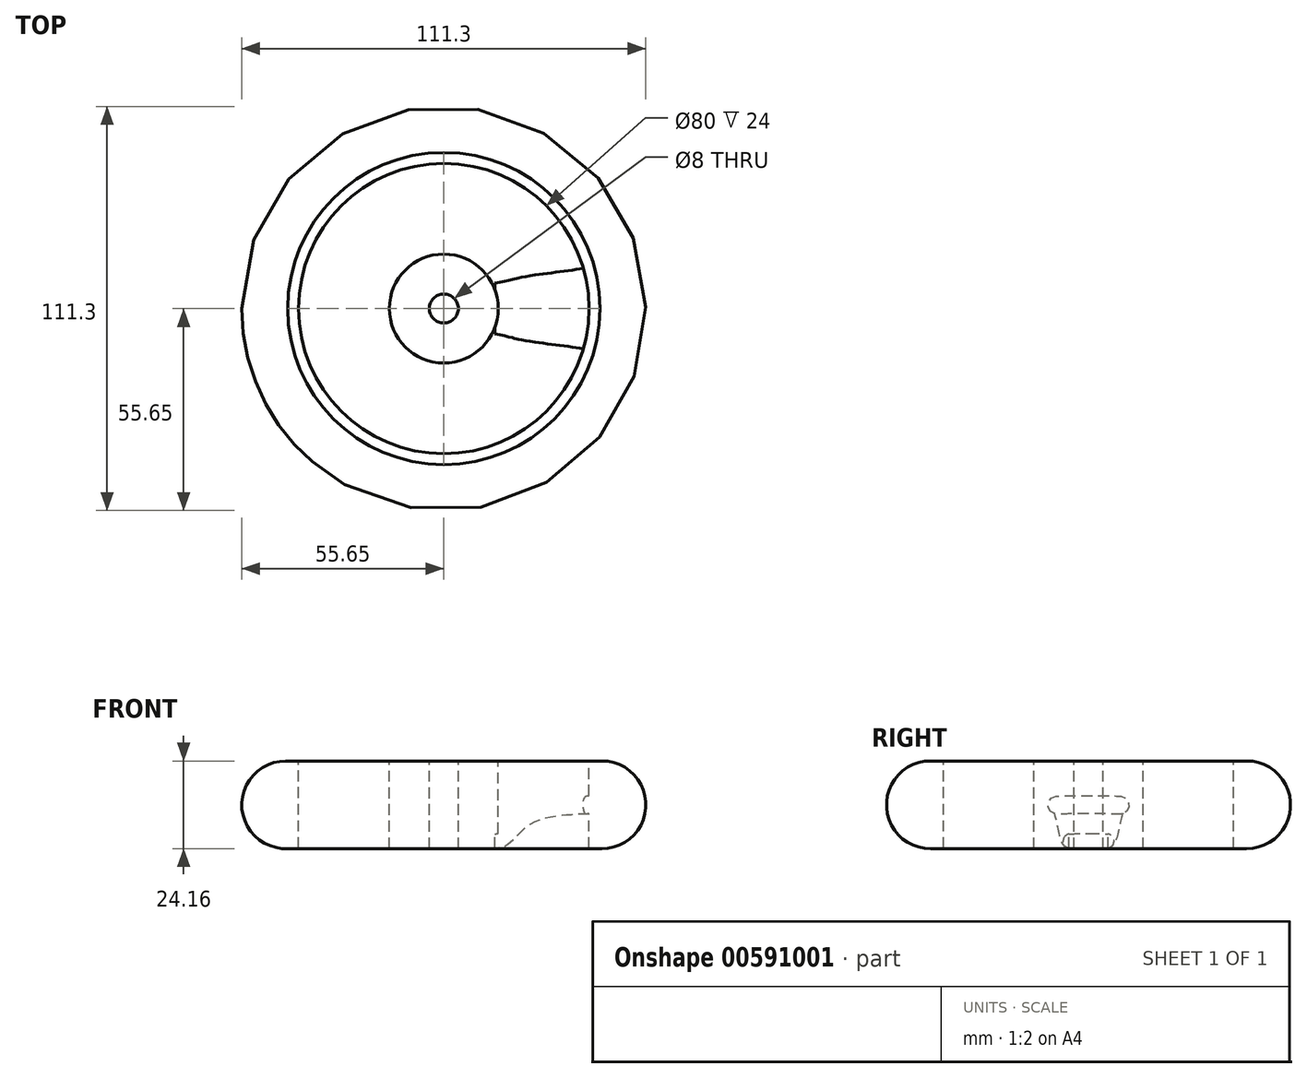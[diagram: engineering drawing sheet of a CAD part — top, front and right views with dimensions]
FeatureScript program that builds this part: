
annotation { "Feature Type Name" : "Feature", "Feature Type Description" : "" }
export const myFeature = defineFeature(function(context is Context, id is Id, definition is map)
    precondition{}
    {
        {
            var Q0;
            Q0=qCreatedBy(makeId("Top.planeOp"),FACE);
            var sketch = newSketch(context, id + "F0", { "sketchPlane" : qUnion([Q0])});
            skCircle(sketch, "E0", {"center": v(0, 0) * mm, "radius": 40 * mm});
            skSolve(sketch);
        }
        {
            var Q0;
            Q0=qCreatedBy(makeId("Front.planeOp"),FACE);
            var sketch = newSketch(context, id + "F1", { "sketchPlane" : qUnion([Q0])});
            skArc(sketch, "E1", {"start": v(-43, 12.07) * mm, "mid": v(-55.65, 0) * mm, "end": v(-43, -12.07) * mm});
            skLineSegment(sketch, "E2", {"start": v(-43, 12.07) * mm, "end": v(-40, 12.07) * mm});
            skLineSegment(sketch, "E3", {"start": v(-40, 12.07) * mm, "end": v(-40, -11.93) * mm});
            skLineSegment(sketch, "E4", {"start": v(-40, -11.93) * mm, "end": v(-43, -12.07) * mm});
            skSolve(sketch);
        }
        {
            var Q0;
            Q0 = qSketchRegion(id + "F1", true);
            var Q1;
            Q1 = qConstructionFilter(qBodyType(qCreatedBy(id + "F0" ,EDGE), BodyType.WIRE), ConstructionObject.NO);
            sweep(context, id + "F2", {"profiles" : qUnion([Q0]), "path" : qUnion([Q1])});
        }
        {
            var Q0;
            Q0=qCreatedBy(makeId("Right.planeOp"),FACE);
            cPlane(context, id + "F3", {"entities" : qUnion([Q0]), "cplaneType" : CPlaneType.OFFSET, "offset" : 40 * mm, "width" : 150 * mm, "height" : 150 * mm});
        }
        {
            var Q0;
            Q0=qCreatedBy(makeId("Right.planeOp"),FACE);
            cPlane(context, id + "F4", {"entities" : qUnion([Q0]), "cplaneType" : CPlaneType.OFFSET, "offset" : 14 * mm, "width" : 150 * mm, "height" : 150 * mm});
        }
        {
            var Q0;
            Q0=qCreatedBy(id+"F3.planeOp",FACE);
            var sketch = newSketch(context, id + "F5", { "sketchPlane" : qUnion([Q0])});
            skLineSegment(sketch, "E5", {"start": v(-9, 0) * mm, "end": v(9, 0) * mm});
            skArc(sketch, "E6.0.startCap", {"start": v(-9, -2.5) * mm, "mid": v(-11.5, 0) * mm, "end": v(-9, 2.5) * mm});
            skArc(sketch, "E6.0.endCap", {"start": v(9, 2.5) * mm, "mid": v(11.5, 0) * mm, "end": v(9, -2.5) * mm});
            skLineSegment(sketch, "E6.0.left", {"start": v(-9, 2.5) * mm, "end": v(9, 2.5) * mm});
            skLineSegment(sketch, "E6.0.right", {"start": v(-9, -2.5) * mm, "end": v(9, -2.5) * mm});
            skSolve(sketch);
        }
        {
            var Q0;
            Q0=qCreatedBy(id+"F4.planeOp",FACE);
            var sketch = newSketch(context, id + "F6", { "sketchPlane" : qUnion([Q0])});
            skLineSegment(sketch, "E7", {"start": v(-5, -10) * mm, "end": v(5, -10) * mm});
            skArc(sketch, "E8.0.startCap", {"start": v(-5, -12) * mm, "mid": v(-7, -10) * mm, "end": v(-5, -8) * mm});
            skArc(sketch, "E8.0.endCap", {"start": v(5, -8) * mm, "mid": v(7, -10) * mm, "end": v(5, -12) * mm});
            skLineSegment(sketch, "E8.0.left", {"start": v(-5, -8) * mm, "end": v(5, -8) * mm});
            skLineSegment(sketch, "E8.0.right", {"start": v(-5, -12) * mm, "end": v(5, -12) * mm});
            skSolve(sketch);
        }
        {
            var Q0;
            Q0=qCreatedBy(makeId("Front.planeOp"),FACE);
            var sketch = newSketch(context, id + "F7", { "sketchPlane" : qUnion([Q0])});
            skFitSpline(sketch, "E9", {"points": [v(14, -12) * mm, v(18.37, -10.38) * mm, v(24.16, -5.17) * mm, v(34.82, -2.8) * mm, v(40, -2.5) * mm], "startDerivative": vector(27.3, -0.01) * mm, "endDerivative": vector(15.84, 0.13) * mm});
            skSolve(sketch);
        }
        {
            var Q1;
            Q1 = qSketchRegion(id + "F5", true);
            var Q2;
            Q2 = qSketchRegion(id + "F6", true);
            var Q3;
            Q3 = qConstructionFilter(qBodyType(qCreatedBy(id + "F7" ,EDGE), BodyType.WIRE), ConstructionObject.NO);
            loft(context, id + "F8", {"operationType" : NewBodyOperationType.ADD, "addGuides" : true, "sheetProfilesArray" : [{ "sheetProfileEntities" : qUnion([Q1]) }, { "sheetProfileEntities" : qUnion([Q2]) }], "guidesArray" : [{ "guideEntities" : qUnion([Q3]), "guideDerivativeType" : LoftGuideDerivativeType.DEFAULT, "guideDerivativeMagnitude" : 1 }]});
        }
        {
            var Q0;
            Q0=qCreatedBy(makeId("Front.planeOp"),FACE);
            var sketch = newSketch(context, id + "F9", { "sketchPlane" : qUnion([Q0])});
            skLineSegment(sketch, "E10.bottom", {"start": v(0, 12) * mm, "end": v(15, 12) * mm});
            skLineSegment(sketch, "E10.top", {"start": v(0, -12) * mm, "end": v(15, -12) * mm});
            skLineSegment(sketch, "E10.left", {"start": v(0, 12) * mm, "end": v(0, -12) * mm});
            skLineSegment(sketch, "E10.right", {"start": v(15, 12) * mm, "end": v(15, -12) * mm});
            skSolve(sketch);
        }
        {
            var Q0;
            Q0 = qSketchRegion(id + "F9", true);
            var Q1;
            Q1=sQuery(id+"F9.wireOp",EDGE,"E10.left");
            revolve(context, id + "F10", {"operationType" : NewBodyOperationType.ADD, "surfaceOperationType" : NewSurfaceOperationType.NEW, "entities" : qUnion([Q0]), "axis" : qUnion([Q1]), "revolveType" : RevolveType.FULL});
        }
        {
            var Q0;
            Q0=makeQuery(id+"F10.opRevolve","SWEPT_FACE",FACE,{"disambiguationData":[OSD([sQuery(id+"F9.wireOp",EDGE,"E10.bottom")])]});
            var sketch = newSketch(context, id + "F11", { "sketchPlane" : qUnion([Q0])});
            skPoint(sketch, "E11", {"position": v(0, 0) * mm});
            skSolve(sketch);
        }
        {
            var Q0;
            Q0=sQuery(id+"F11.wireOp",VERTEX,"E11");
            var Q1;
            Q1=makeQuery(id+"F2.opSweep","SWEPT_BODY",BODY,{"disambiguationData":[OSD([sQuery(id+"F0.wireOp",EDGE,"E0"),sQuery(id+"F1.wireOp",EDGE,"E1"),sQuery(id+"F1.wireOp",EDGE,"E2"),sQuery(id+"F1.wireOp",EDGE,"E3"),sQuery(id+"F1.wireOp",EDGE,"E4")])]});
            hole(context, id + "F12", {"style" : HoleStyle.SIMPLE, "endStyle" : HoleEndStyle.THROUGH, "holeDiameter" : 8 * mm, "majorDiameter" : 5 * mm, "isTappedThrough" : true, "tappedDepth" : 12 * mm, "tapClearance" : 3, "locations" : qUnion([Q0]), "scope" : qUnion([Q1])});
        }
    });
